# Revit family: result
name_source: partatom
category: Furniture
revit_build: Autodesk Revit 2015 (Build: 20140903_1530(x64)
units: mm (PartAtom-declared; Revit-internal decimal feet)

## types (1)
- Default
    BIMobject category = Mirrors
    BIMobject category code = sanitary-mirrors
    BIMobject main category = Sanitary
    BIMobject main category code = sanitary
    Brand url = http://www.delabie.com
    Design country = France
    Edition number = 1
    GTIN code = https://3456330163583
    IFC Classification = Furnishing Element
    Installation instructions = https://www.delabie.com
    Manufacturer country = France
    Manufacturer name = DELABIE
    Material main = Glass
    OmniClass Code = 23-21 37 13 15
    OmniClass Description = Mirrors
    Product Guid = 98fc4953-1e79-414b-9365-0f561040e5b6
    Product SKU = 510202P
    Product data url = https://bimobject.com
    Product family = Sanitary
    Product group = Accessibility
    Product name = 510202P Tilting glass mirror with handle
    Product url = https://www.delabie.com
    QR code = http://bimobject.com
    Technical description = https://www.delabie.com
    UNSPSC Code = 56
    Uniclass 2015 Code = Pr_25_71_53
    Uniclass 2015 Name = Mirrors

## geometry (parser evidence)
native form markers: Sweep x4
no freeform markers — native parametric forms only
